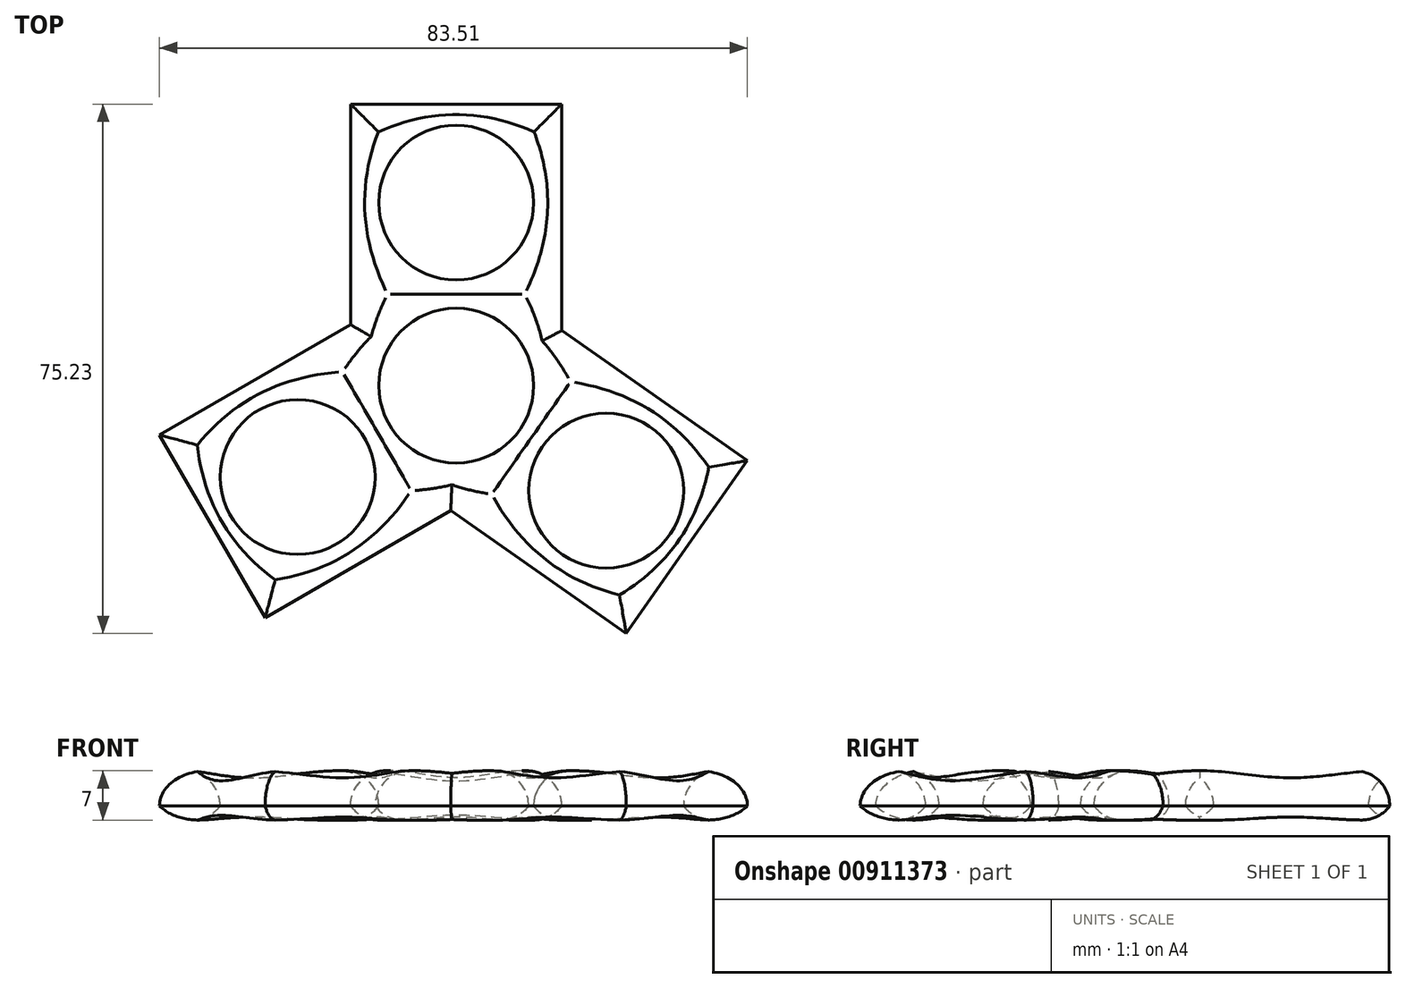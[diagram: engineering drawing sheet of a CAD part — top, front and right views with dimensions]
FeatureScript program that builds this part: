
annotation { "Feature Type Name" : "Feature", "Feature Type Description" : "" }
export const myFeature = defineFeature(function(context is Context, id is Id, definition is map)
    precondition{}
    {
        {
            var Q0;
            Q0=qCreatedBy(makeId("Top.planeOp"),FACE);
            var sketch = newSketch(context, id + "F0", { "sketchPlane" : qUnion([Q0])});
            skCircle(sketch, "E0", {"center": v(0, 0) * mm, "radius": 11 * mm});
            skLineSegment(sketch, "E1.bottom", {"start": v(0, 0) * mm, "end": v(-15, 0) * mm});
            skLineSegment(sketch, "E1.top", {"start": v(0, 40) * mm, "end": v(-15, 40) * mm});
            skLineSegment(sketch, "E1.left", {"start": v(0, 0) * mm, "end": v(0, 40) * mm});
            skLineSegment(sketch, "E1.right", {"start": v(-15, 0) * mm, "end": v(-15, 40) * mm});
            skLineSegment(sketch, "E2.bottom", {"start": v(0, 0) * mm, "end": v(15, 0) * mm});
            skLineSegment(sketch, "E2.top", {"start": v(0, 40) * mm, "end": v(15, 40) * mm});
            skLineSegment(sketch, "E2.right", {"start": v(15, 0) * mm, "end": v(15, 40) * mm});
            skLineSegment(sketch, "E3", {"start": v(0, 40) * mm, "end": v(0, 26) * mm});
            skLineSegment(sketch, "E4", {"start": v(0, 26) * mm, "end": v(0, 40) * mm});
            skCircle(sketch, "E5", {"center": v(0, 26) * mm, "radius": 11 * mm});
            skSolve(sketch);
        }
        {
            var Q0;
            {var subQ0=sQuery(id+"F0.wireOp",EDGE,"E1.top");Q0=makeQuery(id+"F0.imprint","IMPRINT",FACE,{"disambiguationData":[TD([[makeQuery(id+"F0.imprint","IMPRINT",EDGE,{"derivedFrom":subQ0}),1.0]])]});}
            var Q1;
            {var subQ7=sQuery(id+"F0.wireOp",EDGE,"E2.top");Q1=makeQuery(id+"F0.imprint","IMPRINT",FACE,{"disambiguationData":[TD([[makeQuery(id+"F0.imprint","IMPRINT",EDGE,{"derivedFrom":subQ7}),-1.0]])]});}
            extrude(context, id + "F1", {"entities" : qUnion([Q0, Q1]), "depth" : 7 * mm, "offsetDistance" : 25 * mm});
        }
        {
            var Q0;
            Q0=qCreatedBy(makeId("Front.planeOp"),FACE);
            var sketch = newSketch(context, id + "F2", { "sketchPlane" : qUnion([Q0])});
            skLineSegment(sketch, "E6", {"start": v(0, 0) * mm, "end": v(0, 31.63) * mm});
            skSolve(sketch);
        }
        {
            var Q0;
            Q0=makeQuery(id+"F1.opExtrude","SWEPT_BODY",BODY,{"disambiguationData":[OSD([sQuery(id+"F0.wireOp",EDGE,"E0"),sQuery(id+"F0.wireOp",EDGE,"E1.bottom"),sQuery(id+"F0.wireOp",EDGE,"E1.top"),sQuery(id+"F0.wireOp",EDGE,"E1.right"),sQuery(id+"F0.wireOp",EDGE,"E2.bottom"),sQuery(id+"F0.wireOp",EDGE,"E2.top"),sQuery(id+"F0.wireOp",EDGE,"E2.right"),sQuery(id+"F0.wireOp",EDGE,"E5")])]});
            var Q1;
            Q1=sQuery(id+"F2.wireOp",EDGE,"E6");
            transform(context, id + "F3", {"entities" : qUnion([Q0]), "transformType" : TransformType.ROTATION, "transformAxis" : qUnion([Q1]), "angle" : 120 * degree, "makeCopy" : true});
        }
        {
            var Q0;
            Q0=makeQuery(id+"F1.opExtrude","SWEPT_BODY",BODY,{"disambiguationData":[OSD([sQuery(id+"F0.wireOp",EDGE,"E0"),sQuery(id+"F0.wireOp",EDGE,"E1.bottom"),sQuery(id+"F0.wireOp",EDGE,"E1.top"),sQuery(id+"F0.wireOp",EDGE,"E1.right"),sQuery(id+"F0.wireOp",EDGE,"E2.bottom"),sQuery(id+"F0.wireOp",EDGE,"E2.top"),sQuery(id+"F0.wireOp",EDGE,"E2.right"),sQuery(id+"F0.wireOp",EDGE,"E5")])]});
            var Q1;
            Q1=sQuery(id+"F2.wireOp",EDGE,"E6");
            transform(context, id + "F4", {"entities" : qUnion([Q0]), "transformType" : TransformType.ROTATION, "transformAxis" : qUnion([Q1]), "angle" : 125 * degree, "oppositeDirection" : true, "makeCopy" : true});
        }
        {
            var Q0;
            Q0=makeQuery(id+"F3.opPattern","COPY",BODY,{"derivedFrom":makeQuery(id+"F1.opExtrude","SWEPT_BODY",BODY,{"disambiguationData":[OSD([sQuery(id+"F0.wireOp",EDGE,"E0"),sQuery(id+"F0.wireOp",EDGE,"E1.bottom"),sQuery(id+"F0.wireOp",EDGE,"E1.top"),sQuery(id+"F0.wireOp",EDGE,"E1.right"),sQuery(id+"F0.wireOp",EDGE,"E2.bottom"),sQuery(id+"F0.wireOp",EDGE,"E2.top"),sQuery(id+"F0.wireOp",EDGE,"E2.right"),sQuery(id+"F0.wireOp",EDGE,"E5")])]}),"instanceName":"1"});
            var Q1;
            Q1=makeQuery(id+"F4.opPattern","COPY",BODY,{"derivedFrom":makeQuery(id+"F1.opExtrude","SWEPT_BODY",BODY,{"disambiguationData":[OSD([sQuery(id+"F0.wireOp",EDGE,"E0"),sQuery(id+"F0.wireOp",EDGE,"E1.bottom"),sQuery(id+"F0.wireOp",EDGE,"E1.top"),sQuery(id+"F0.wireOp",EDGE,"E1.right"),sQuery(id+"F0.wireOp",EDGE,"E2.bottom"),sQuery(id+"F0.wireOp",EDGE,"E2.top"),sQuery(id+"F0.wireOp",EDGE,"E2.right"),sQuery(id+"F0.wireOp",EDGE,"E5")])]}),"instanceName":"1"});
            var Q2;
            Q2=makeQuery(id+"F1.opExtrude","SWEPT_BODY",BODY,{"disambiguationData":[OSD([sQuery(id+"F0.wireOp",EDGE,"E0"),sQuery(id+"F0.wireOp",EDGE,"E1.bottom"),sQuery(id+"F0.wireOp",EDGE,"E1.top"),sQuery(id+"F0.wireOp",EDGE,"E1.right"),sQuery(id+"F0.wireOp",EDGE,"E2.bottom"),sQuery(id+"F0.wireOp",EDGE,"E2.top"),sQuery(id+"F0.wireOp",EDGE,"E2.right"),sQuery(id+"F0.wireOp",EDGE,"E5")])]});
            booleanBodies(context, id + "F5", {"operationType" : BooleanOperationType.UNION, "tools" : qUnion([Q0, Q1, Q2])});
        }
        {
            var Q0;
            {var subQ0=makeQuery(id+"F1.opExtrude","CAP_FACE",FACE,{"disambiguationData":[OSD([sQuery(id+"F0.wireOp",EDGE,"E0"),sQuery(id+"F0.wireOp",EDGE,"E1.bottom"),sQuery(id+"F0.wireOp",EDGE,"E1.top"),sQuery(id+"F0.wireOp",EDGE,"E1.right"),sQuery(id+"F0.wireOp",EDGE,"E2.bottom"),sQuery(id+"F0.wireOp",EDGE,"E2.top"),sQuery(id+"F0.wireOp",EDGE,"E2.right"),sQuery(id+"F0.wireOp",EDGE,"E5")])],"isStart":false});Q0=makeQuery(id+"F5.opBoolean","MERGE",FACE,{"derivedFrom":[subQ0,makeQuery(id+"F3.opPattern","COPY",FACE,{"derivedFrom":subQ0,"instanceName":"1"}),makeQuery(id+"F4.opPattern","COPY",FACE,{"derivedFrom":subQ0,"instanceName":"1"})]});}
            fillet(context, id + "F6", {"entities" : qUnion([Q0]), "radius" : 5 * mm, "tangentPropagation" : true, "allowEdgeOverflow" : false});
        }
        {
            var Q0;
            {var subQ0=makeQuery(id+"F1.opExtrude","CAP_FACE",FACE,{"disambiguationData":[OSD([sQuery(id+"F0.wireOp",EDGE,"E0"),sQuery(id+"F0.wireOp",EDGE,"E1.bottom"),sQuery(id+"F0.wireOp",EDGE,"E1.top"),sQuery(id+"F0.wireOp",EDGE,"E1.right"),sQuery(id+"F0.wireOp",EDGE,"E2.bottom"),sQuery(id+"F0.wireOp",EDGE,"E2.top"),sQuery(id+"F0.wireOp",EDGE,"E2.right"),sQuery(id+"F0.wireOp",EDGE,"E5")])],"isStart":true});Q0=makeQuery(id+"F5.opBoolean","MERGE",FACE,{"derivedFrom":[subQ0,makeQuery(id+"F3.opPattern","COPY",FACE,{"derivedFrom":subQ0,"instanceName":"1"}),makeQuery(id+"F4.opPattern","COPY",FACE,{"derivedFrom":subQ0,"instanceName":"1"})]});}
            fillet(context, id + "F7", {"entities" : qUnion([Q0]), "radius" : 5 * mm, "tangentPropagation" : true, "allowEdgeOverflow" : false});
        }
    });
